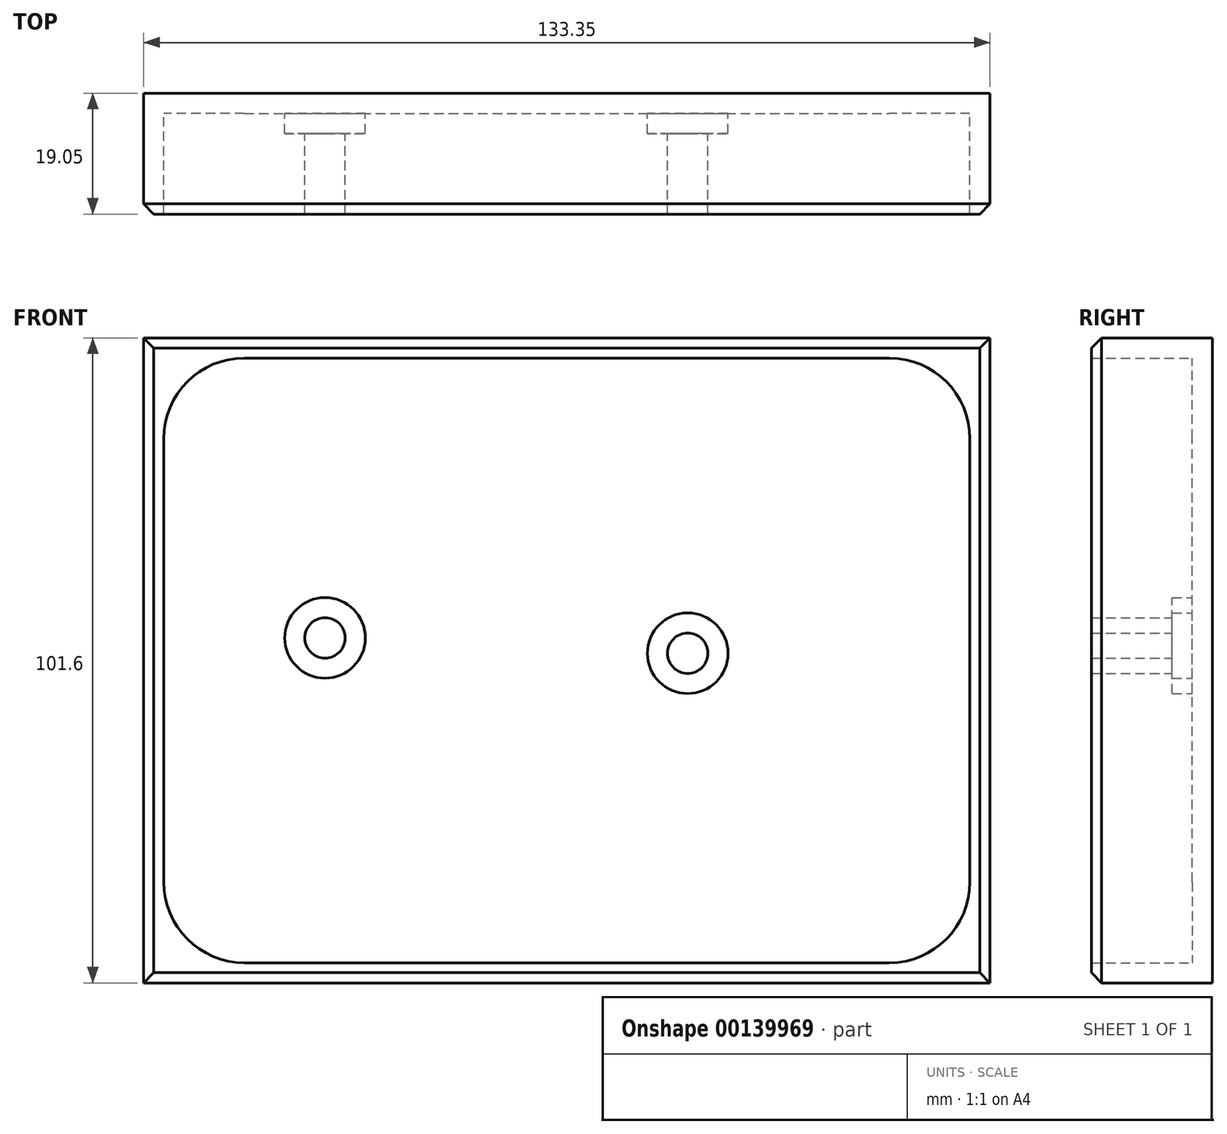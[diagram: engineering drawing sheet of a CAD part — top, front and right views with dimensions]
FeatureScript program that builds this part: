
annotation { "Feature Type Name" : "Feature", "Feature Type Description" : "" }
export const myFeature = defineFeature(function(context is Context, id is Id, definition is map)
    precondition{}
    {
        {
            var Q0;
            Q0=qCreatedBy(makeId("Front.planeOp"),FACE);
            var sketch = newSketch(context, id + "F0", { "sketchPlane" : qUnion([Q0])});
            skLineSegment(sketch, "E0.bottom", {"start": v(0, 0) * mm, "end": v(133.35, 0) * mm});
            skLineSegment(sketch, "E0.top", {"start": v(0, 101.6) * mm, "end": v(133.35, 101.6) * mm});
            skLineSegment(sketch, "E0.left", {"start": v(0, 0) * mm, "end": v(0, 101.6) * mm});
            skLineSegment(sketch, "E0.right", {"start": v(133.35, 0) * mm, "end": v(133.35, 101.6) * mm});
            skSolve(sketch);
        }
        {
            var Q0;
            Q0 = qSketchRegion(id + "F0", true);
            extrude(context, id + "F1", {"entities" : qUnion([Q0]), "depth" : 19.05 * mm});
        }
        {
            var Q0;
            Q0=makeQuery(id+"F1.opExtrude","CAP_FACE",FACE,{"disambiguationData":[OSD([sQuery(id+"F0.wireOp",EDGE,"E0.bottom"),sQuery(id+"F0.wireOp",EDGE,"E0.top"),sQuery(id+"F0.wireOp",EDGE,"E0.left"),sQuery(id+"F0.wireOp",EDGE,"E0.right")])],"isStart":false});
            shell(context, id + "F2", {"entities" : qUnion([Q0]), "thickness" : 3.17 * mm});
        }
        {
            var Q0;
            Q0=makeQuery(id+"F2.opShell","OFFSET_FACE",FACE,{"disambiguationData":[OSD([sQuery(id+"F0.wireOp",EDGE,"E0.bottom"),sQuery(id+"F0.wireOp",EDGE,"E0.top"),sQuery(id+"F0.wireOp",EDGE,"E0.left"),sQuery(id+"F0.wireOp",EDGE,"E0.right")])]});
            var sketch = newSketch(context, id + "F3", { "sketchPlane" : qUnion([Q0])});
            skCircle(sketch, "E1", {"center": v(28.58, 54.35) * mm, "radius": 6.35 * mm});
            skCircle(sketch, "E2", {"center": v(85.73, 51.92) * mm, "radius": 6.35 * mm});
            skLineSegment(sketch, "E3", {"start": v(28.58, 54.35) * mm, "end": v(3.18, 54.35) * mm, "construction": true});
            skSolve(sketch);
        }
        {
            var Q0;
            Q0 = qSketchRegion(id + "F3", true);
            extrude(context, id + "F4", {"entities" : qUnion([Q0]), "operationType" : NewBodyOperationType.ADD, "depth" : 3.17 * mm});
        }
        {
            var Q0;
            Q0=makeQuery(id+"F2.opShell","OFFSET_FACE",FACE,{"disambiguationData":[OSD([sQuery(id+"F0.wireOp",EDGE,"E0.bottom"),sQuery(id+"F0.wireOp",EDGE,"E0.top"),sQuery(id+"F0.wireOp",EDGE,"E0.left"),sQuery(id+"F0.wireOp",EDGE,"E0.right")])]});
            var sketch = newSketch(context, id + "F5", { "sketchPlane" : qUnion([Q0])});
            skCircle(sketch, "E4", {"center": v(28.58, 54.35) * mm, "radius": 3.18 * mm});
            skCircle(sketch, "E5", {"center": v(85.73, 51.92) * mm, "radius": 3.18 * mm});
            skSolve(sketch);
        }
        {
            var Q0;
            Q0 = qSketchRegion(id + "F5", true);
            extrude(context, id + "F6", {"entities" : qUnion([Q0]), "operationType" : NewBodyOperationType.ADD, "depth" : 15.88 * mm});
        }
        {
            var Q0;
            Q0=makeQuery(id+"F2.opShell","OFFSET_EDGE",EDGE,{"disambiguationData":[OSD([sQuery(id+"F0.wireOp",EDGE,"E0.bottom"),sQuery(id+"F0.wireOp",EDGE,"E0.left")])]});
            var Q1;
            Q1=makeQuery(id+"F2.opShell","OFFSET_EDGE",EDGE,{"disambiguationData":[OSD([sQuery(id+"F0.wireOp",EDGE,"E0.top"),sQuery(id+"F0.wireOp",EDGE,"E0.left")])]});
            var Q2;
            Q2=makeQuery(id+"F2.opShell","OFFSET_EDGE",EDGE,{"disambiguationData":[OSD([sQuery(id+"F0.wireOp",EDGE,"E0.bottom"),sQuery(id+"F0.wireOp",EDGE,"E0.right")])]});
            var Q3;
            Q3=makeQuery(id+"F2.opShell","OFFSET_EDGE",EDGE,{"disambiguationData":[OSD([sQuery(id+"F0.wireOp",EDGE,"E0.top"),sQuery(id+"F0.wireOp",EDGE,"E0.right")])]});
            fillet(context, id + "F7", {"entities" : qUnion([Q0, Q1, Q2, Q3]), "radius" : 12.7 * mm, "tangentPropagation" : true, "allowEdgeOverflow" : false});
        }
        {
            var Q0;
            Q0=makeQuery(id+"F1.opExtrude","CAP_EDGE",EDGE,{"disambiguationData":[OSD([sQuery(id+"F0.wireOp",EDGE,"E0.right")])],"isStart":false});
            var Q1;
            Q1=makeQuery(id+"F1.opExtrude","CAP_EDGE",EDGE,{"disambiguationData":[OSD([sQuery(id+"F0.wireOp",EDGE,"E0.bottom")])],"isStart":false});
            var Q2;
            Q2=makeQuery(id+"F1.opExtrude","CAP_EDGE",EDGE,{"disambiguationData":[OSD([sQuery(id+"F0.wireOp",EDGE,"E0.left")])],"isStart":false});
            var Q3;
            Q3=makeQuery(id+"F1.opExtrude","CAP_EDGE",EDGE,{"disambiguationData":[OSD([sQuery(id+"F0.wireOp",EDGE,"E0.top")])],"isStart":false});
            chamfer(context, id + "F8", {"entities" : qUnion([Q0, Q1, Q2, Q3]), "width" : 1.6 * mm, "tangentPropagation" : true});
        }
    });
